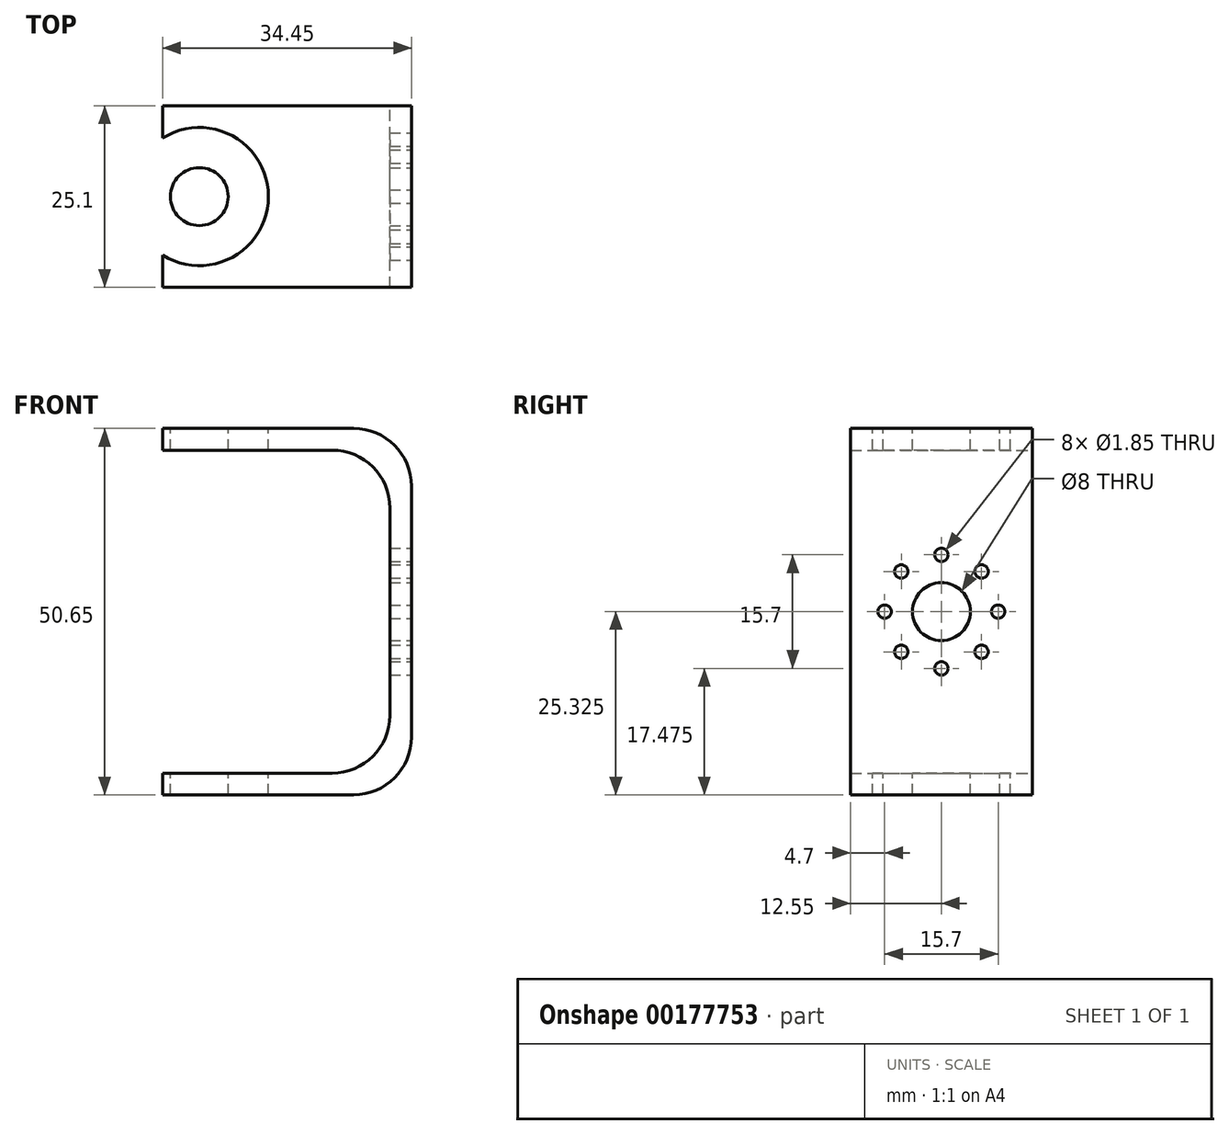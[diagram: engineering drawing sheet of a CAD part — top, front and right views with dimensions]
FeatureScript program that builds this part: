
annotation { "Feature Type Name" : "Feature", "Feature Type Description" : "" }
export const myFeature = defineFeature(function(context is Context, id is Id, definition is map)
    precondition{}
    {
        {
            var Q0;
            Q0=qCreatedBy(makeId("Top.planeOp"),FACE);
            var sketch = newSketch(context, id + "F0", { "sketchPlane" : qUnion([Q0])});
            skLineSegment(sketch, "E0.bottom", {"start": v(-15.32, 25.1) * mm, "end": v(19.13, 25.1) * mm});
            skLineSegment(sketch, "E0.top", {"start": v(-15.32, 0) * mm, "end": v(19.13, 0) * mm});
            skLineSegment(sketch, "E0.left", {"start": v(-15.32, 25.1) * mm, "end": v(-15.32, 0) * mm});
            skLineSegment(sketch, "E0.right", {"start": v(19.13, 25.1) * mm, "end": v(19.13, 0) * mm});
            skSolve(sketch);
        }
        {
            var Q0;
            Q0=qSketchRegion(id+"F0",true);
            extrude(context, id + "F1", {"entities" : qUnion([Q0]), "depth" : 50.65 * mm});
        }
        {
            var Q0;
            Q0=makeQuery(id+"F1.opExtrude","SWEPT_FACE",FACE,{"disambiguationData":[OSD([sQuery(id+"F0.wireOp",EDGE,"E0.left")])]});
            shell(context, id + "F2", {"entities" : qUnion([Q0]), "thickness" : 5 * mm});
        }
        {
            var Q0;
            Q0=makeQuery(id+"F1.opExtrude","SWEPT_FACE",FACE,{"disambiguationData":[OSD([sQuery(id+"F0.wireOp",EDGE,"E0.right")])]});
            var sketch = newSketch(context, id + "F3", { "sketchPlane" : qUnion([Q0])});
            skLineSegment(sketch, "E1", {"start": v(12.55, 0) * mm, "end": v(12.55, 50.65) * mm, "construction": true});
            skCircle(sketch, "E2", {"center": v(12.55, 25.32) * mm, "radius": 4 * mm});
            skCircle(sketch, "E3", {"center": v(12.55, 17.48) * mm, "radius": 0.93 * mm});
            skCircle(sketch, "E4.1.0", {"center": v(18.1, 19.77) * mm, "radius": 0.92 * mm});
            skCircle(sketch, "E4.2.0", {"center": v(20.4, 25.32) * mm, "radius": 0.93 * mm});
            skCircle(sketch, "E4.3.0", {"center": v(18.1, 30.88) * mm, "radius": 0.93 * mm});
            skCircle(sketch, "E5.1.4.0", {"center": v(12.55, 33.18) * mm, "radius": 0.93 * mm});
            skCircle(sketch, "E5.1.5.0", {"center": v(7, 30.88) * mm, "radius": 0.93 * mm});
            skCircle(sketch, "E5.1.6.0", {"center": v(4.7, 25.32) * mm, "radius": 0.92 * mm});
            skCircle(sketch, "E5.1.7.0", {"center": v(7, 19.77) * mm, "radius": 0.93 * mm});
            skSolve(sketch);
        }
        {
            var Q0;
            Q0=qSketchRegion(id+"F3",true);
            extrude(context, id + "F4", {"entities" : qUnion([Q0]), "operationType" : NewBodyOperationType.REMOVE, "oppositeDirection" : true, "depth" : 25 * mm});
        }
        {
            var Q0;
            Q0=makeQuery(id+"F1.opExtrude","SWEPT_FACE",FACE,{"disambiguationData":[OSD([sQuery(id+"F0.wireOp",EDGE,"E0.bottom")])]});
            var sketch = newSketch(context, id + "F5", { "sketchPlane" : qUnion([Q0])});
            skLineSegment(sketch, "E6", {"start": v(15.32, 3) * mm, "end": v(-16.13, 3) * mm});
            skLineSegment(sketch, "E7", {"start": v(-16.13, 3) * mm, "end": v(-16.13, 47.65) * mm});
            skLineSegment(sketch, "E8", {"start": v(-16.13, 47.65) * mm, "end": v(15.32, 47.65) * mm});
            skSolve(sketch);
        }
        {
            var Q0;
            {var subQ0=sQuery(id+"F5.wireOp",EDGE,"E6");Q0=makeQuery(id+"F5.imprint","IMPRINT",FACE,{"disambiguationData":[TD([[makeQuery(id+"F5.imprint","IMPRINT",EDGE,{"derivedFrom":subQ0}),-1.0]])]});}
            extrude(context, id + "F6", {"entities" : qUnion([Q0]), "operationType" : NewBodyOperationType.REMOVE, "endBound" : BoundingType.THROUGH_ALL, "oppositeDirection" : true, "depth" : 25 * mm});
        }
        {
            var Q0;
            Q0=makeQuery(id+"F6.boolean.opBoolean","COPY",EDGE,{"derivedFrom":makeQuery(id+"F6.opExtrude","SWEPT_EDGE",EDGE,{"disambiguationData":[OSD([sQuery(id+"F5.wireOp",EDGE,"E7"),sQuery(id+"F5.wireOp",EDGE,"E8")])]})});
            var Q1;
            Q1=makeQuery(id+"F6.boolean.opBoolean","COPY",EDGE,{"derivedFrom":makeQuery(id+"F6.opExtrude","SWEPT_EDGE",EDGE,{"disambiguationData":[OSD([sQuery(id+"F5.wireOp",EDGE,"E6"),sQuery(id+"F5.wireOp",EDGE,"E7")])]})});
            fillet(context, id + "F7", {"entities" : qUnion([Q0, Q1]), "radius" : 8 * mm, "tangentPropagation" : true, "allowEdgeOverflow" : false});
        }
        {
            var Q0;
            Q0=makeQuery(id+"F1.opExtrude","CAP_EDGE",EDGE,{"disambiguationData":[OSD([sQuery(id+"F0.wireOp",EDGE,"E0.right")])],"isStart":false});
            var Q1;
            Q1=makeQuery(id+"F1.opExtrude","CAP_EDGE",EDGE,{"disambiguationData":[OSD([sQuery(id+"F0.wireOp",EDGE,"E0.right")])],"isStart":true});
            fillet(context, id + "F8", {"entities" : qUnion([Q0, Q1]), "radius" : 8 * mm, "tangentPropagation" : true, "allowEdgeOverflow" : false});
        }
        {
            var Q0;
            Q0=makeQuery(id+"F1.opExtrude","CAP_FACE",FACE,{"disambiguationData":[OSD([sQuery(id+"F0.wireOp",EDGE,"E0.bottom"),sQuery(id+"F0.wireOp",EDGE,"E0.top"),sQuery(id+"F0.wireOp",EDGE,"E0.left"),sQuery(id+"F0.wireOp",EDGE,"E0.right")])],"isStart":false});
            var sketch = newSketch(context, id + "F9", { "sketchPlane" : qUnion([Q0])});
            skLineSegment(sketch, "E9", {"start": v(-15.32, 0) * mm, "end": v(-15.32, 25.1) * mm, "construction": true});
            skLineSegment(sketch, "E10", {"start": v(19.13, 25.1) * mm, "end": v(19.13, 0) * mm, "construction": true});
            skLineSegment(sketch, "E11", {"start": v(16.13, 0) * mm, "end": v(16.13, 25.1) * mm, "construction": true});
            skLineSegment(sketch, "E12.0", {"start": v(-15.32, 3) * mm, "end": v(19.13, 3) * mm});
            skLineSegment(sketch, "E12.1", {"start": v(-15.32, 3) * mm, "end": v(-15.32, 22.1) * mm});
            skLineSegment(sketch, "E12.2", {"start": v(-15.32, 22.1) * mm, "end": v(19.13, 22.1) * mm});
            skLineSegment(sketch, "E13", {"start": v(-15.32, 12.55) * mm, "end": v(19.13, 12.55) * mm});
            skPoint(sketch, "E13.endSnap0", {"position": v(-15.32, 12.55) * mm});
            skCircle(sketch, "E14", {"center": v(-10.22, 12.55) * mm, "radius": 4 * mm});
            skCircle(sketch, "E15", {"center": v(-10.22, 12.55) * mm, "radius": 9.55 * mm});
            skCircle(sketch, "E16", {"center": v(-3.12, 12.55) * mm, "radius": 0.93 * mm});
            skPoint(sketch, "E17", {"position": v(-0.67, 12.55) * mm});
            skCircle(sketch, "E18.1.0", {"center": v(-10.22, 19.65) * mm, "radius": 0.93 * mm});
            skCircle(sketch, "E18.2.0", {"center": v(-17.32, 12.55) * mm, "radius": 0.93 * mm});
            skCircle(sketch, "E18.3.0", {"center": v(-10.22, 5.45) * mm, "radius": 0.93 * mm});
            skLineSegment(sketch, "E19", {"start": v(-10.22, 8.55) * mm, "end": v(-18.9, 8.55) * mm});
            skLineSegment(sketch, "E20", {"start": v(-10.22, 16.55) * mm, "end": v(-15.32, 16.55) * mm});
            skLineSegment(sketch, "E21", {"start": v(19.13, 22.1) * mm, "end": v(-15.32, 22.1) * mm, "construction": true});
            skLineSegment(sketch, "E22", {"start": v(-15.32, 3) * mm, "end": v(19.13, 3) * mm, "construction": true});
            skSolve(sketch);
        }
        {
            var Q0;
            Q0=makeQuery(id+"F9.imprint","IMPRINT",FACE,{"disambiguationData":[TD([[makeQuery(id+"F9.imprint","IMPRINT",EDGE,{"derivedFrom":sQuery(id+"F9.wireOp",EDGE,"E18.1.0")}),1.0]])]});
            var Q1;
            Q1=makeQuery(id+"F9.imprint","IMPRINT",FACE,{"disambiguationData":[TD([[makeQuery(id+"F9.imprint","IMPRINT",EDGE,{"derivedFrom":sQuery(id+"F9.wireOp",EDGE,"E18.3.0")}),1.0]])]});
            var Q2;
            {var subQ0=sQuery(id+"F9.wireOp",EDGE,"E16");var subQ1=sQuery(id+"F9.wireOp",EDGE,"E13");var subQ2=makeQuery(id+"F9.imprint","INTERSECT",VERTEX,{"disambiguationData":[OD(0.0)],"derivedFrom":[subQ1,subQ0]});Q2=makeQuery(id+"F9.imprint","IMPRINT",FACE,{"disambiguationData":[TD([[makeQuery(id+"F9.imprint","IMPRINT",EDGE,{"disambiguationData":[TD([[subQ2,-1.0]])],"derivedFrom":subQ1}),1.0]])]});}
            var Q3;
            {var subQ0=sQuery(id+"F9.wireOp",EDGE,"E16");var subQ1=sQuery(id+"F9.wireOp",EDGE,"E13");var subQ2=makeQuery(id+"F9.imprint","INTERSECT",VERTEX,{"disambiguationData":[OD(0.0)],"derivedFrom":[subQ1,subQ0]});Q3=makeQuery(id+"F9.imprint","IMPRINT",FACE,{"disambiguationData":[TD([[makeQuery(id+"F9.imprint","IMPRINT",EDGE,{"disambiguationData":[TD([[subQ2,-1.0]])],"derivedFrom":subQ1}),-1.0]])]});}
            var Q4;
            {var subQ0=sQuery(id+"F9.wireOp",EDGE,"E14");var subQ1=sQuery(id+"F9.wireOp",EDGE,"E13");var subQ2=makeQuery(id+"F9.imprint","INTERSECT",VERTEX,{"disambiguationData":[OD(0.0)],"derivedFrom":[subQ1,subQ0]});Q4=makeQuery(id+"F9.imprint","IMPRINT",FACE,{"disambiguationData":[TD([[makeQuery(id+"F9.imprint","IMPRINT",EDGE,{"disambiguationData":[TD([[subQ2,-1.0]])],"derivedFrom":subQ1}),1.0]])]});}
            var Q5;
            {var subQ0=sQuery(id+"F9.wireOp",EDGE,"E14");var subQ1=sQuery(id+"F9.wireOp",EDGE,"E13");var subQ2=makeQuery(id+"F9.imprint","INTERSECT",VERTEX,{"disambiguationData":[OD(0.0)],"derivedFrom":[subQ1,subQ0]});Q5=makeQuery(id+"F9.imprint","IMPRINT",FACE,{"disambiguationData":[TD([[makeQuery(id+"F9.imprint","IMPRINT",EDGE,{"disambiguationData":[TD([[subQ2,-1.0]])],"derivedFrom":subQ1}),-1.0]])]});}
            var Q6;
            {var subQ3=sQuery(id+"F9.wireOp",EDGE,"E20");Q6=makeQuery(id+"F9.imprint","IMPRINT",FACE,{"disambiguationData":[TD([[makeQuery(id+"F9.imprint","IMPRINT",EDGE,{"derivedFrom":subQ3}),1.0]])]});}
            var Q7;
            {var subQ0=sQuery(id+"F9.wireOp",EDGE,"E13");var subQ1=sQuery(id+"F9.wireOp",EDGE,"E12.1");var subQ2=makeQuery(id+"F9.imprint","INTERSECT",VERTEX,{"derivedFrom":[subQ1,subQ0]});Q7=makeQuery(id+"F9.imprint","IMPRINT",FACE,{"disambiguationData":[TD([[makeQuery(id+"F9.imprint","IMPRINT",EDGE,{"disambiguationData":[TD([[subQ2,-1.0]])],"derivedFrom":subQ1}),1.0]])]});}
            extrude(context, id + "F10", {"entities" : qUnion([Q0, Q1, Q2, Q3, Q4, Q5, Q6, Q7]), "operationType" : NewBodyOperationType.REMOVE, "endBound" : BoundingType.THROUGH_ALL, "oppositeDirection" : true, "depth" : 25 * mm});
        }
    });
